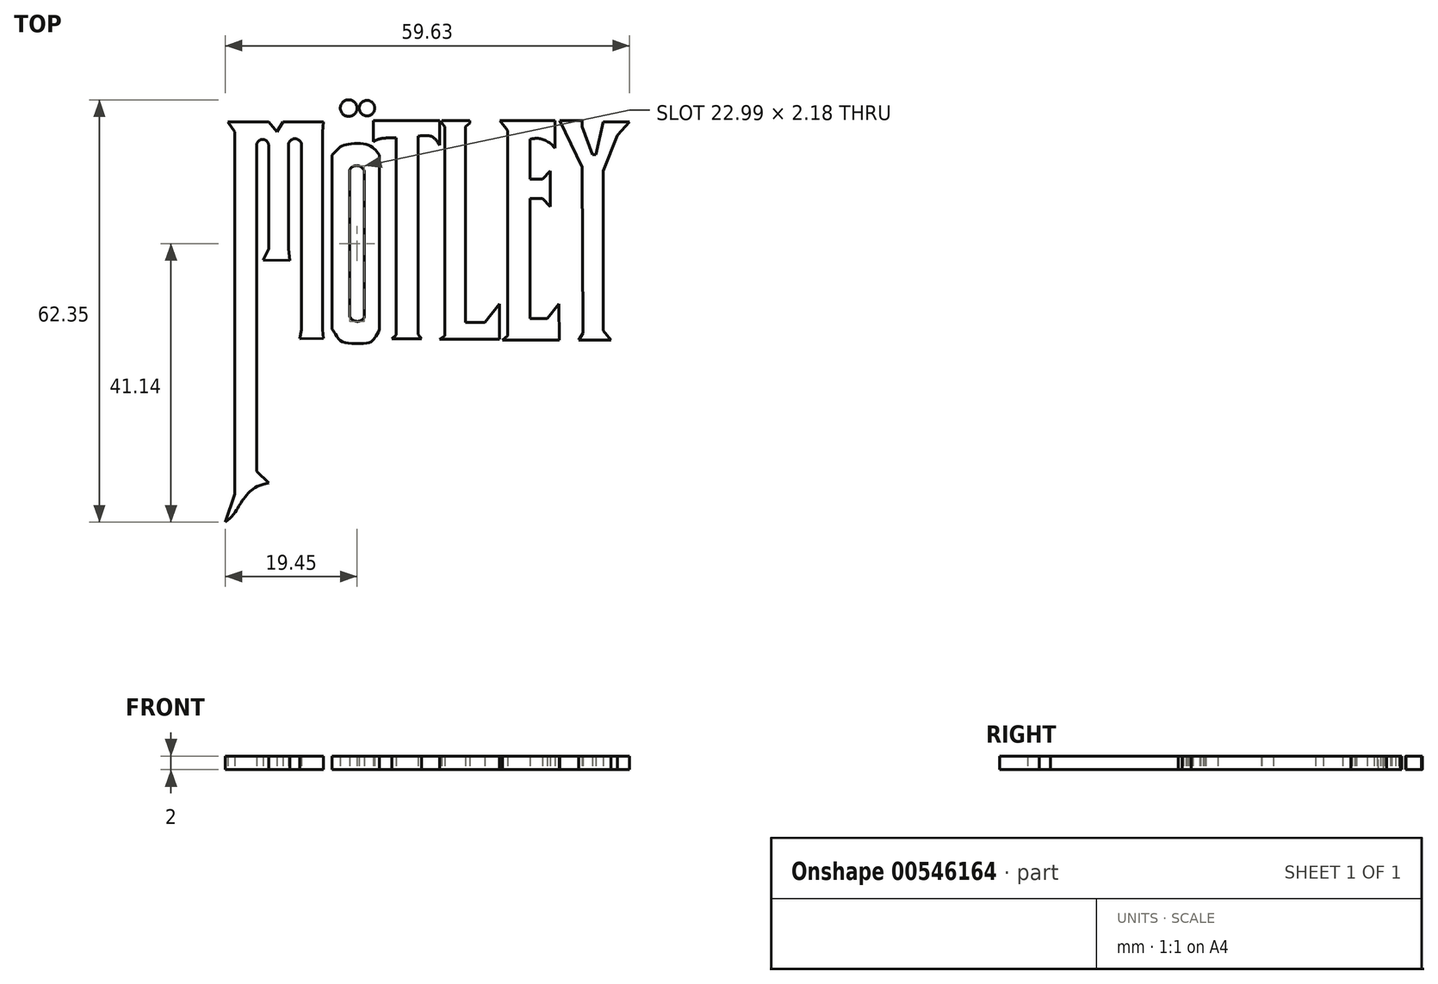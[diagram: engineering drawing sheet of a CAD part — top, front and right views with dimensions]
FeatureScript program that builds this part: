
annotation { "Feature Type Name" : "Feature", "Feature Type Description" : "" }
export const myFeature = defineFeature(function(context is Context, id is Id, definition is map)
    precondition{}
    {
        {
            var Q0;
            Q0=qCreatedBy(makeId("Top.planeOp"),FACE);
            var sketch = newSketch(context, id + "F0", { "sketchPlane" : qUnion([Q0])});
            skLineSegment(sketch, "E0", {"start": v(-57.86, -10.31) * mm, "end": v(-56.45, -6.15) * mm});
            skLineSegment(sketch, "E1", {"start": v(-56.45, -6.15) * mm, "end": v(-56.45, 47.32) * mm});
            skLineSegment(sketch, "E2", {"start": v(-56.45, 47.32) * mm, "end": v(-57.46, 48.77) * mm});
            skLineSegment(sketch, "E3", {"start": v(-57.46, 48.77) * mm, "end": v(-51.46, 48.77) * mm});
            skLineSegment(sketch, "E4", {"start": v(-51.46, 48.77) * mm, "end": v(-50.21, 47.32) * mm});
            skLineSegment(sketch, "E5", {"start": v(-50.21, 47.32) * mm, "end": v(-49.32, 48.77) * mm});
            skLineSegment(sketch, "E6", {"start": v(-49.32, 48.77) * mm, "end": v(-43.37, 48.77) * mm});
            skLineSegment(sketch, "E7", {"start": v(-43.37, 48.77) * mm, "end": v(-43.52, 47.32) * mm});
            skLineSegment(sketch, "E8", {"start": v(-43.52, 47.32) * mm, "end": v(-43.52, 18.1) * mm});
            skLineSegment(sketch, "E9", {"start": v(-43.52, 18.1) * mm, "end": v(-43.37, 16.82) * mm});
            skLineSegment(sketch, "E10", {"start": v(-46.85, 16.79) * mm, "end": v(-46.6, 18.1) * mm});
            skLineSegment(sketch, "E11", {"start": v(-46.6, 18.1) * mm, "end": v(-46.6, 45.32) * mm});
            skLineSegment(sketch, "E12", {"start": v(-48.54, 45.32) * mm, "end": v(-48.54, 30.06) * mm});
            skLineSegment(sketch, "E13", {"start": v(-48.54, 30.06) * mm, "end": v(-48.34, 28.3) * mm});
            skLineSegment(sketch, "E14", {"start": v(-52.24, 28.37) * mm, "end": v(-51.46, 30.06) * mm});
            skLineSegment(sketch, "E15", {"start": v(-51.46, 30.06) * mm, "end": v(-51.46, 45.32) * mm});
            skLineSegment(sketch, "E16", {"start": v(-53.22, 45.32) * mm, "end": v(-53.22, -2.81) * mm});
            skLineSegment(sketch, "E17", {"start": v(-53.22, -2.81) * mm, "end": v(-51.46, -4.5) * mm});
            skArc(sketch, "E18", {"start": v(-51.46, 45.32) * mm, "mid": v(-52.34, 46.2) * mm, "end": v(-53.22, 45.32) * mm});
            skArc(sketch, "E19", {"start": v(-46.6, 45.32) * mm, "mid": v(-47.57, 46.3) * mm, "end": v(-48.54, 45.32) * mm});
            skFitSpline(sketch, "E20", {"points": [v(-57.86, -10.31) * mm, v(-56.56, -9.07) * mm, v(-55.9, -7.97) * mm, v(-55.32, -7.1) * mm, v(-54.53, -6.13) * mm, v(-53.7, -5.37) * mm, v(-51.46, -4.5) * mm], "startDerivative": vector(7.4, 6) * mm, "endDerivative": vector(19.69, 5.13) * mm});
            skLineSegment(sketch, "E21", {"start": v(-46.85, 16.79) * mm, "end": v(-43.37, 16.82) * mm});
            skLineSegment(sketch, "E22", {"start": v(-52.24, 28.37) * mm, "end": v(-48.34, 28.3) * mm});
            skLineSegment(sketch, "E23", {"start": v(-42.08, 43.9) * mm, "end": v(-42.08, 18.18) * mm});
            skLineSegment(sketch, "E24", {"start": v(-35.1, 18.18) * mm, "end": v(-35.1, 43.9) * mm});
            skFitSpline(sketch, "E25", {"points": [v(-42.08, 43.9) * mm, v(-40.99, 45) * mm, v(-39.78, 45.48) * mm, v(-37.28, 45.5) * mm, v(-35.96, 44.88) * mm, v(-35.1, 43.9) * mm], "startDerivative": vector(5.83, 4.95) * mm, "endDerivative": vector(4.46, -5.79) * mm});
            skFitSpline(sketch, "E26", {"points": [v(-42.08, 18.18) * mm, v(-41.66, 17.6) * mm, v(-40.91, 16.53) * mm, v(-39.24, 16.09) * mm, v(-36.76, 16.16) * mm, v(-36.1, 16.53) * mm, v(-35.69, 17.03) * mm, v(-35.1, 18.18) * mm], "startDerivative": vector(3.7, -4.53) * mm, "endDerivative": vector(4.12, 8.58) * mm});
            skArc(sketch, "E27", {"start": v(-37.35, 41.58) * mm, "mid": v(-38.38, 42.33) * mm, "end": v(-39.49, 41.68) * mm});
            skArc(sketch, "E28", {"start": v(-39.5, 20.12) * mm, "mid": v(-38.45, 19.33) * mm, "end": v(-37.32, 20) * mm});
            skLineSegment(sketch, "E29", {"start": v(-39.5, 20.12) * mm, "end": v(-39.49, 41.68) * mm});
            skLineSegment(sketch, "E30", {"start": v(-37.35, 41.58) * mm, "end": v(-37.32, 20) * mm});
            skCircle(sketch, "E31", {"center": v(-39.65, 50.81) * mm, "radius": 1.23 * mm});
            skPoint(sketch, "E31.first.point", {"position": v(-40.87, 50.64) * mm});
            skPoint(sketch, "E31.second.point", {"position": v(-38.42, 50.86) * mm});
            skPoint(sketch, "E31.third.point", {"position": v(-38.42, 50.76) * mm});
            skCircle(sketch, "E32", {"center": v(-36.94, 50.8) * mm, "radius": 1.14 * mm});
            skPoint(sketch, "E32.first.point", {"position": v(-38.08, 50.86) * mm});
            skPoint(sketch, "E32.second.point", {"position": v(-35.8, 50.86) * mm});
            skPoint(sketch, "E32.third.point", {"position": v(-36.27, 49.88) * mm});
            skFitSpline(sketch, "E33", {"points": [v(-36, 45.86) * mm, v(-36, 48.97) * mm], "startDerivative": vector(0, 3.11) * mm, "endDerivative": vector(0, 3.11) * mm});
            skFitSpline(sketch, "E34", {"points": [v(-36, 48.97) * mm, v(-26.25, 48.97) * mm], "startDerivative": vector(9.74, 0) * mm, "endDerivative": vector(9.74, 0) * mm});
            skLineSegment(sketch, "E35", {"start": v(-26.25, 48.97) * mm, "end": v(-26.25, 45.36) * mm});
            skFitSpline(sketch, "E36", {"points": [v(-26.25, 45.36) * mm, v(-27.36, 46.59) * mm, v(-29.4, 46.67) * mm], "startDerivative": vector(-1.97, 3.15) * mm, "endDerivative": vector(-4.27, -0.47) * mm});
            skFitSpline(sketch, "E37", {"points": [v(-36, 45.86) * mm, v(-34.95, 46.3) * mm, v(-32.62, 46.41) * mm], "startDerivative": vector(2.26, 1.24) * mm, "endDerivative": vector(4.36, -0.06) * mm});
            skLineSegment(sketch, "E38", {"start": v(-32.62, 46.41) * mm, "end": v(-32.62, 17.36) * mm});
            skLineSegment(sketch, "E39", {"start": v(-29.4, 46.67) * mm, "end": v(-29.4, 17.4) * mm});
            skLineSegment(sketch, "E40", {"start": v(-29.4, 17.4) * mm, "end": v(-28.91, 16.79) * mm});
            skLineSegment(sketch, "E41", {"start": v(-28.91, 16.79) * mm, "end": v(-33.28, 16.79) * mm});
            skLineSegment(sketch, "E42", {"start": v(-33.28, 16.79) * mm, "end": v(-32.62, 17.36) * mm});
            skLineSegment(sketch, "E43", {"start": v(-25.45, 48.1) * mm, "end": v(-25.89, 48.57) * mm});
            skLineSegment(sketch, "E44", {"start": v(-25.89, 48.57) * mm, "end": v(-25.89, 48.97) * mm});
            skLineSegment(sketch, "E45", {"start": v(-25.89, 48.97) * mm, "end": v(-21.8, 48.97) * mm});
            skLineSegment(sketch, "E46", {"start": v(-21.8, 48.97) * mm, "end": v(-21.8, 48.57) * mm});
            skLineSegment(sketch, "E47", {"start": v(-21.8, 48.57) * mm, "end": v(-22.4, 48.1) * mm});
            skLineSegment(sketch, "E48", {"start": v(-22.4, 48.1) * mm, "end": v(-22.4, 19.2) * mm});
            skLineSegment(sketch, "E49", {"start": v(-22.4, 19.2) * mm, "end": v(-19.53, 19.2) * mm});
            skLineSegment(sketch, "E50", {"start": v(-19.53, 19.2) * mm, "end": v(-17.4, 21.89) * mm});
            skLineSegment(sketch, "E51", {"start": v(-17.4, 21.89) * mm, "end": v(-17.4, 16.73) * mm});
            skLineSegment(sketch, "E52", {"start": v(-17.4, 16.73) * mm, "end": v(-26.25, 16.73) * mm});
            skLineSegment(sketch, "E53", {"start": v(-26.25, 16.73) * mm, "end": v(-25.45, 17.22) * mm});
            skLineSegment(sketch, "E54", {"start": v(-25.45, 17.22) * mm, "end": v(-25.45, 48.1) * mm});
            skLineSegment(sketch, "E55", {"start": v(-8.55, 16.61) * mm, "end": v(-16.97, 16.61) * mm});
            skLineSegment(sketch, "E56", {"start": v(-16.97, 16.61) * mm, "end": v(-16.2, 17.2) * mm});
            skLineSegment(sketch, "E57", {"start": v(-16.2, 17.2) * mm, "end": v(-16.2, 47.52) * mm});
            skLineSegment(sketch, "E58", {"start": v(-16.2, 47.52) * mm, "end": v(-17.33, 48.97) * mm});
            skLineSegment(sketch, "E59", {"start": v(-17.33, 48.97) * mm, "end": v(-9.22, 48.97) * mm});
            skLineSegment(sketch, "E60", {"start": v(-9.22, 48.97) * mm, "end": v(-9.22, 44.9) * mm});
            skFitSpline(sketch, "E61", {"points": [v(-9.22, 44.9) * mm, v(-11.3, 46.27) * mm, v(-12.92, 46.23) * mm], "startDerivative": vector(-1.97, 3.15) * mm, "endDerivative": vector(-4.27, -0.47) * mm});
            skLineSegment(sketch, "E62", {"start": v(-12.92, 46.23) * mm, "end": v(-12.92, 40.31) * mm});
            skLineSegment(sketch, "E63", {"start": v(-12.92, 40.31) * mm, "end": v(-11.05, 40.31) * mm});
            skLineSegment(sketch, "E64", {"start": v(-11.05, 40.31) * mm, "end": v(-9.91, 41.51) * mm});
            skLineSegment(sketch, "E65", {"start": v(-9.91, 41.51) * mm, "end": v(-9.91, 36.28) * mm});
            skLineSegment(sketch, "E66", {"start": v(-9.91, 36.28) * mm, "end": v(-11.05, 37.46) * mm});
            skLineSegment(sketch, "E67", {"start": v(-11.05, 37.46) * mm, "end": v(-12.92, 37.46) * mm});
            skLineSegment(sketch, "E68", {"start": v(-12.92, 37.46) * mm, "end": v(-12.92, 19.74) * mm});
            skLineSegment(sketch, "E69", {"start": v(-12.92, 19.74) * mm, "end": v(-10.36, 19.74) * mm});
            skLineSegment(sketch, "E70", {"start": v(-10.36, 19.74) * mm, "end": v(-8.66, 21.89) * mm});
            skLineSegment(sketch, "E71", {"start": v(-8.66, 21.89) * mm, "end": v(-8.55, 16.61) * mm});
            skLineSegment(sketch, "E72", {"start": v(-5.73, 16.58) * mm, "end": v(-0.93, 16.58) * mm});
            skLineSegment(sketch, "E73", {"start": v(-0.93, 16.58) * mm, "end": v(-2.09, 17.96) * mm});
            skLineSegment(sketch, "E74", {"start": v(-2.09, 17.96) * mm, "end": v(-2.09, 41.51) * mm});
            skLineSegment(sketch, "E75", {"start": v(-2.09, 41.51) * mm, "end": v(0, 46.8) * mm});
            skLineSegment(sketch, "E76", {"start": v(0, 46.8) * mm, "end": v(1.77, 48.78) * mm});
            skLineSegment(sketch, "E77", {"start": v(1.77, 48.78) * mm, "end": v(-2.09, 48.78) * mm});
            skLineSegment(sketch, "E78", {"start": v(-2.09, 48.78) * mm, "end": v(-3.2, 43.93) * mm});
            skLineSegment(sketch, "E79", {"start": v(-3.2, 43.93) * mm, "end": v(-3.67, 43.93) * mm});
            skLineSegment(sketch, "E80", {"start": v(-3.67, 43.93) * mm, "end": v(-5.21, 48.09) * mm});
            skLineSegment(sketch, "E81", {"start": v(-5.21, 48.09) * mm, "end": v(-5.21, 48.97) * mm});
            skLineSegment(sketch, "E82", {"start": v(-5.21, 48.97) * mm, "end": v(-8.52, 48.97) * mm});
            skLineSegment(sketch, "E83", {"start": v(-8.52, 48.97) * mm, "end": v(-5.21, 42.08) * mm});
            skLineSegment(sketch, "E84", {"start": v(-5.21, 42.08) * mm, "end": v(-5.08, 17.62) * mm});
            skLineSegment(sketch, "E85", {"start": v(-5.08, 17.62) * mm, "end": v(-5.73, 16.58) * mm});
            skSolve(sketch);
        }
        {
            var Q0;
            Q0 = qSketchRegion(id + "F0", true);
            extrude(context, id + "F1", {"entities" : qUnion([Q0]), "depth" : 2 * mm, "offsetDistance" : 25.4 * mm});
        }
    });
